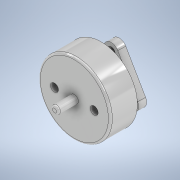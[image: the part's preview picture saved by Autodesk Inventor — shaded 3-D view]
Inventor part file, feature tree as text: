
AUTODESK INVENTOR PART (.ipt)
format: ipt  version: 2021 (Build 250183000, 183)  size: 185,856 bytes
history: native  units: mm
features: extrude x6, sketch x6, fillet x1, chamfer x1
ambient origin geometry x8: Origin, YZ Plane, XZ Plane, XY Plane, X Axis, Y Axis, Z Axis, Center Point
bodies: Solid1 (feature_tree)
feature tree (14):
  extrude  "Extrusion1"  Depth=6.8mm TaperAngle=0.0deg
  extrude  "Extrusion6"  Depth=5.0mm TaperAngle=0.0deg
  extrude  "Extrusion2"  Depth=2.5mm TaperAngle=0.0deg
  extrude  "Extrusion3"  Depth=10.0mm
  extrude  "Extrusion4"  Depth=5.0mm
  extrude  "Extrusion5"  Depth=2.0mm
  fillet  "Fillet1"  Radius=5.773503mm
  chamfer  "Chamfer1"  Distance=12.5mm
  sketch  "Sketch1"  dims[d0=18.15mm d1=6.8mm d2=0.0mm]
  sketch  "Sketch2"  dims[d3=2.0mm d4=5.0mm d5=0.0mm]
  sketch  "Sketch3"  dims[d6=7.0mm d7=2.5mm d8=0.0mm]
  sketch  "Sketch4"  dims[d9=10.0mm d10=10.0mm]
  sketch  "Sketch5"  dims[d11=10.0mm d12=5.0mm]
  sketch  "Sketch6"  dims[d13=2.0mm d17=5.773503mm d18=5.773503mm d19=12.5mm d20=2.0mm d21=0.0mm d22=4.3mm d23=1.6mm d24=0.0mm d25=5.0mm d26=5.0mm d27=2.0mm d28=1.6mm d29=0.0mm d30=0.5mm d31=1.0mm d32=2.0mm d33=45.0deg]
